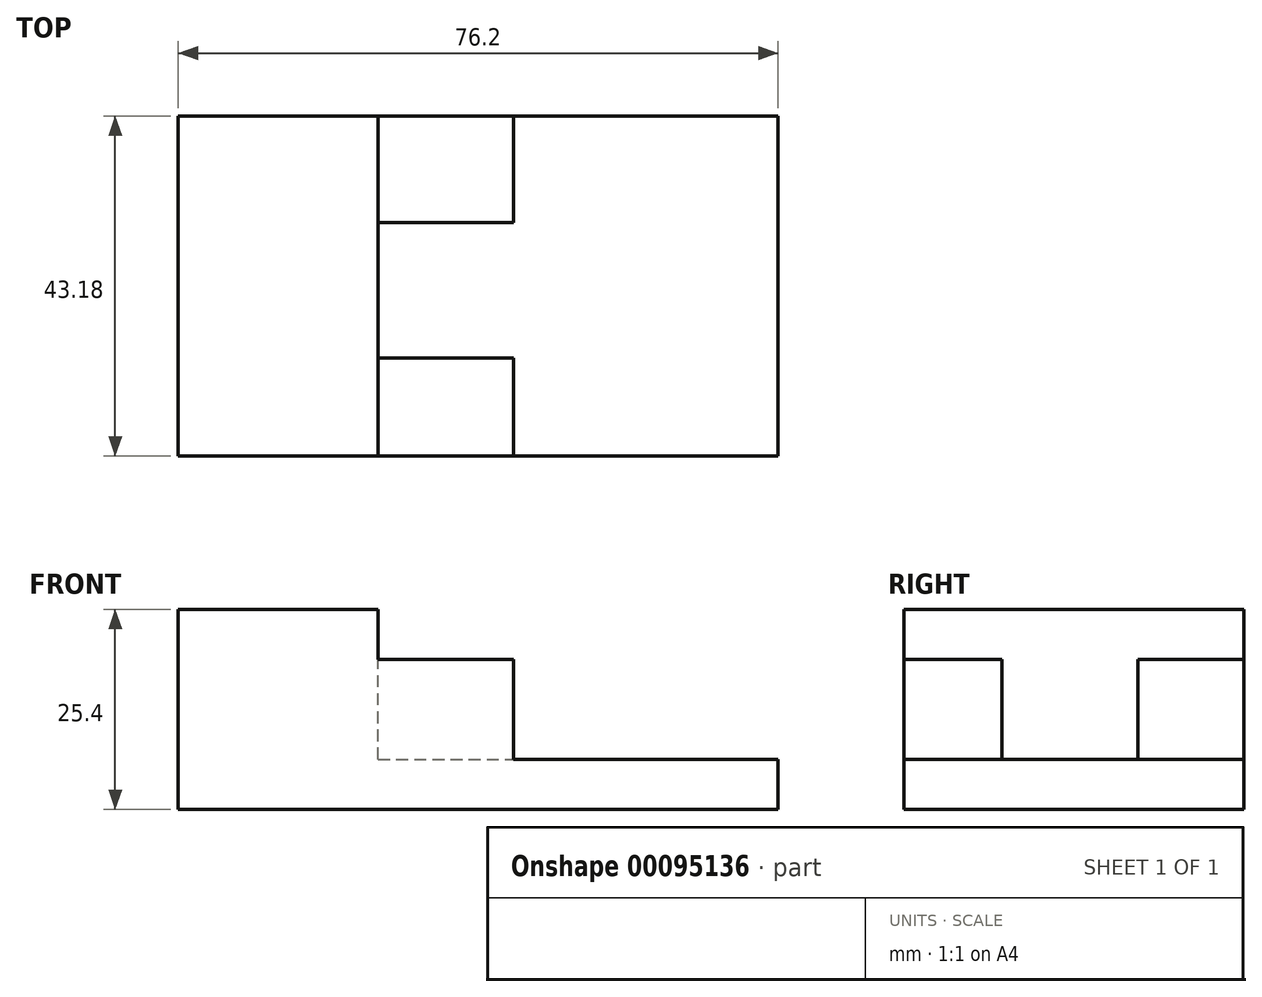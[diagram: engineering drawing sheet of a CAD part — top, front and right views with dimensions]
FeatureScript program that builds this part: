
annotation { "Feature Type Name" : "Feature", "Feature Type Description" : "" }
export const myFeature = defineFeature(function(context is Context, id is Id, definition is map)
    precondition{}
    {
        {
            var Q0;
            Q0=qCreatedBy(makeId("Top.planeOp"),FACE);
            var sketch = newSketch(context, id + "F0", { "sketchPlane" : qUnion([Q0])});
            skLineSegment(sketch, "E0.bottom", {"start": v(-3.43, 11.79) * mm, "end": v(72.77, 11.79) * mm});
            skLineSegment(sketch, "E0.top", {"start": v(-3.43, -31.4) * mm, "end": v(72.77, -31.4) * mm});
            skLineSegment(sketch, "E0.left", {"start": v(-3.43, 11.79) * mm, "end": v(-3.43, -31.4) * mm});
            skLineSegment(sketch, "E0.right", {"start": v(72.77, 11.79) * mm, "end": v(72.77, -31.4) * mm});
            skSolve(sketch);
        }
        {
            var Q0;
            Q0 = qSketchRegion(id + "F0", true);
            extrude(context, id + "F1", {"entities" : qUnion([Q0]), "depth" : 25.4 * mm});
        }
        {
            var Q0;
            Q0=makeQuery(id+"F1.opExtrude","SWEPT_FACE",FACE,{"disambiguationData":[OSD([sQuery(id+"F0.wireOp",EDGE,"E0.top")])]});
            var sketch = newSketch(context, id + "F2", { "sketchPlane" : qUnion([Q0])});
            skLineSegment(sketch, "E1.bottom", {"start": v(21.97, 25.4) * mm, "end": v(72.77, 25.4) * mm});
            skLineSegment(sketch, "E1.top", {"start": v(21.97, 19.05) * mm, "end": v(72.77, 19.05) * mm});
            skLineSegment(sketch, "E1.left", {"start": v(21.97, 25.4) * mm, "end": v(21.97, 19.05) * mm});
            skLineSegment(sketch, "E1.right", {"start": v(72.77, 25.4) * mm, "end": v(72.77, 19.05) * mm});
            skSolve(sketch);
        }
        {
            var Q0;
            Q0=makeQuery(id+"F2.imprint","IMPRINT",FACE,{"disambiguationData":[TD([[makeQuery(id+"F2.imprint","IMPRINT",EDGE,{"derivedFrom":sQuery(id+"F2.wireOp",EDGE,"E1.bottom")}),-1.0]])]});
            extrude(context, id + "F3", {"entities" : qUnion([Q0]), "operationType" : NewBodyOperationType.REMOVE, "endBound" : BoundingType.THROUGH_ALL, "oppositeDirection" : true, "depth" : 25.4 * mm});
        }
        {
            var Q0;
            Q0=makeQuery(id+"F3.boolean.opBoolean","COPY",FACE,{"derivedFrom":makeQuery(id+"F3.opExtrude","SWEPT_FACE",FACE,{"disambiguationData":[OSD([sQuery(id+"F2.wireOp",EDGE,"E1.top")])]})});
            var sketch = newSketch(context, id + "F4", { "sketchPlane" : qUnion([Q0])});
            skLineSegment(sketch, "E2", {"start": v(21.97, -1.7) * mm, "end": v(21.97, -18.97) * mm});
            skLineSegment(sketch, "E3", {"start": v(21.97, -18.97) * mm, "end": v(39.16, -18.97) * mm});
            skLineSegment(sketch, "E4", {"start": v(21.97, -1.7) * mm, "end": v(39.16, -1.7) * mm});
            skLineSegment(sketch, "E5", {"start": v(39.16, -18.97) * mm, "end": v(39.16, -31.4) * mm});
            skLineSegment(sketch, "E6", {"start": v(39.16, -1.7) * mm, "end": v(39.16, 11.79) * mm});
            skLineSegment(sketch, "E7", {"start": v(39.16, 11.79) * mm, "end": v(72.77, 11.79) * mm});
            skLineSegment(sketch, "E8", {"start": v(72.77, 11.79) * mm, "end": v(72.77, -31.4) * mm});
            skLineSegment(sketch, "E9", {"start": v(72.77, -31.4) * mm, "end": v(39.16, -31.4) * mm});
            skSolve(sketch);
        }
        {
            var Q0;
            Q0 = qSketchRegion(id + "F4", true);
            extrude(context, id + "F5", {"entities" : qUnion([Q0]), "operationType" : NewBodyOperationType.REMOVE, "oppositeDirection" : true, "depth" : 12.7 * mm});
        }
    });
